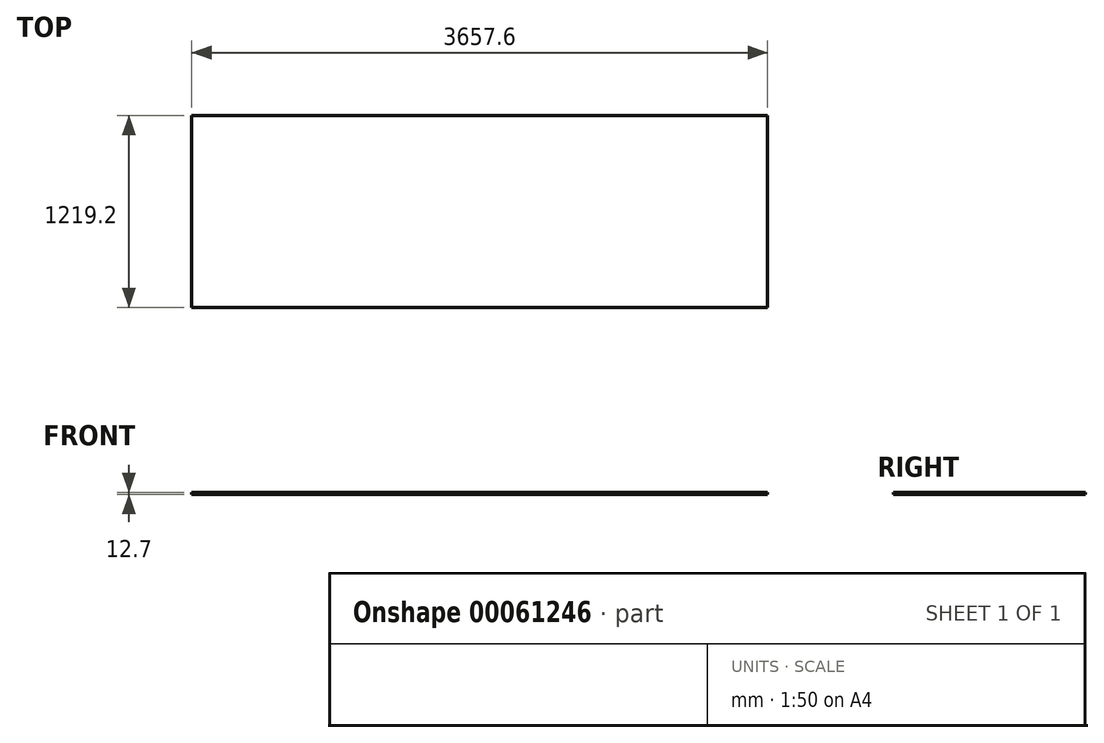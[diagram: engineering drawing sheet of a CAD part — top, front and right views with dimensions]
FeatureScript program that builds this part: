
annotation { "Feature Type Name" : "Feature", "Feature Type Description" : "" }
export const myFeature = defineFeature(function(context is Context, id is Id, definition is map)
    precondition{}
    {
        {
            var Q0;
            Q0=qCreatedBy(makeId("Top.planeOp"),FACE);
            var sketch = newSketch(context, id + "F0", { "sketchPlane" : qUnion([Q0])});
            skLineSegment(sketch, "E0.bottom", {"start": v(0, 0) * mm, "end": v(3657.6, 0) * mm});
            skLineSegment(sketch, "E0.top", {"start": v(0, -1219.2) * mm, "end": v(3657.6, -1219.2) * mm});
            skLineSegment(sketch, "E0.left", {"start": v(0, 0) * mm, "end": v(0, -1219.2) * mm});
            skLineSegment(sketch, "E0.right", {"start": v(3657.6, 0) * mm, "end": v(3657.6, -1219.2) * mm});
            skSolve(sketch);
        }
        {
            var Q0;
            Q0=makeQuery(id+"F0.imprint","IMPRINT",FACE,{"disambiguationData":[TD([[makeQuery(id+"F0.imprint","IMPRINT",EDGE,{"derivedFrom":sQuery(id+"F0.wireOp",EDGE,"E0.bottom")}),-1.0]])]});
            extrude(context, id + "F1", {"entities" : qUnion([Q0]), "depth" : 12.7 * mm});
        }
    });
